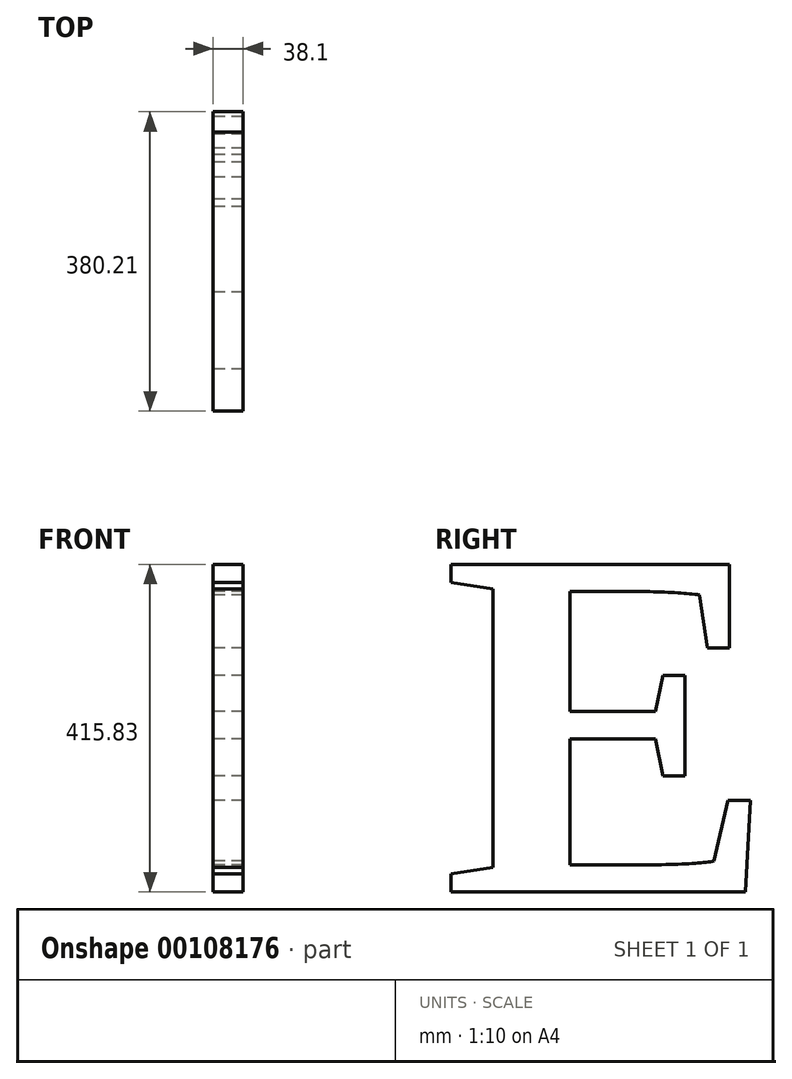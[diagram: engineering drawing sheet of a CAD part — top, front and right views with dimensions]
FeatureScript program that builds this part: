
annotation { "Feature Type Name" : "Feature", "Feature Type Description" : "" }
export const myFeature = defineFeature(function(context is Context, id is Id, definition is map)
    precondition{}
    {
        {
            var Q0;
            Q0=qCreatedBy(makeId("Right.planeOp"),FACE);
            var sketch = newSketch(context, id + "F0", { "sketchPlane" : qUnion([Q0])});
            skText(sketch, "E0", { "text": "E", "fontName": "Tinos-Bold.ttf"});
            skLineSegment(sketch, "E1", {"start": v(-418.9, 11.72) * mm, "end": v(-43.77, 11.72) * mm});
            const initialGuessF0  = {"E0": [-0.4307, 0, 1, 0, 0.4572]};
            skSetInitialGuess(sketch, initialGuessF0);
            skSolve(sketch);
        }
        {
            var Q0;
            Q0 = qSketchRegion(id + "F0", true);
            extrude(context, id + "F1", {"entities" : qUnion([Q0]), "depth" : 38.1 * mm});
        }
    });
